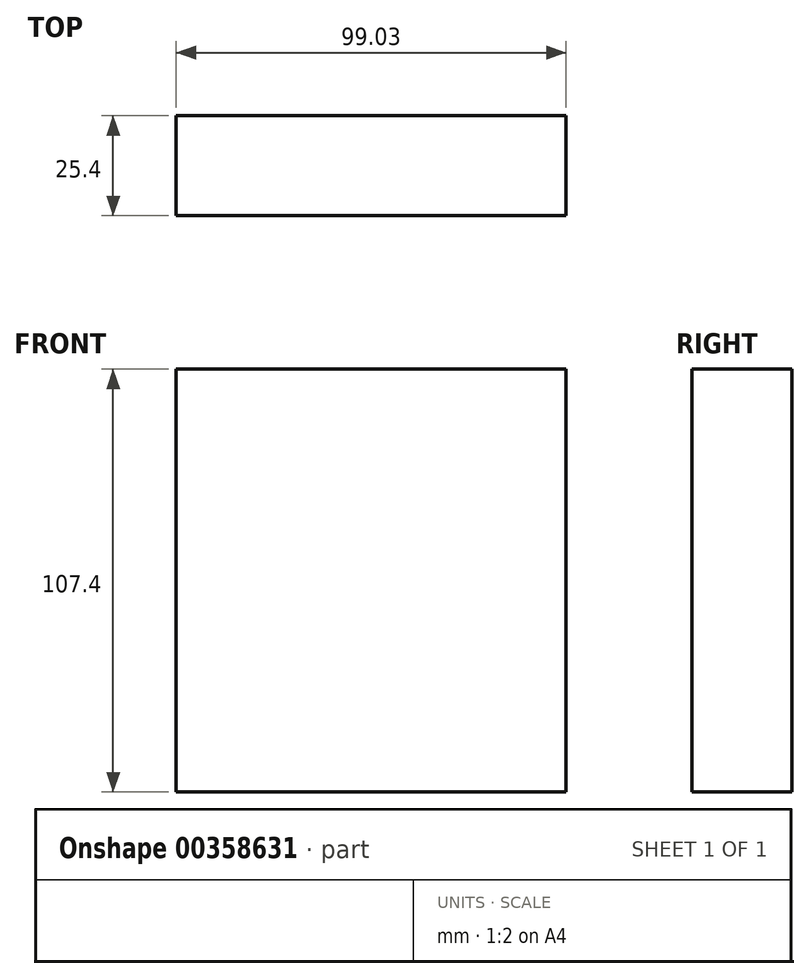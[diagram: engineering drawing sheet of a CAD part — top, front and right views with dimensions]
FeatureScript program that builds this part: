
annotation { "Feature Type Name" : "Feature", "Feature Type Description" : "" }
export const myFeature = defineFeature(function(context is Context, id is Id, definition is map)
    precondition{}
    {
        {
            var Q0;
            Q0=qCreatedBy(makeId("Front.planeOp"),FACE);
            var sketch = newSketch(context, id + "F0", { "sketchPlane" : qUnion([Q0])});
            skLineSegment(sketch, "E0.bottom", {"start": v(-124.8, -4.15) * mm, "end": v(-25.77, -4.15) * mm});
            skLineSegment(sketch, "E0.top", {"start": v(-124.8, -111.55) * mm, "end": v(-25.77, -111.55) * mm});
            skLineSegment(sketch, "E0.left", {"start": v(-124.8, -4.15) * mm, "end": v(-124.8, -111.55) * mm});
            skLineSegment(sketch, "E0.right", {"start": v(-25.77, -4.15) * mm, "end": v(-25.77, -111.55) * mm});
            skSolve(sketch);
        }
        {
            var Q0;
            Q0=qSketchRegion(id+"F0",true);
            extrude(context, id + "F1", {"entities" : qUnion([Q0]), "depth" : 25.4 * mm});
        }
    });
